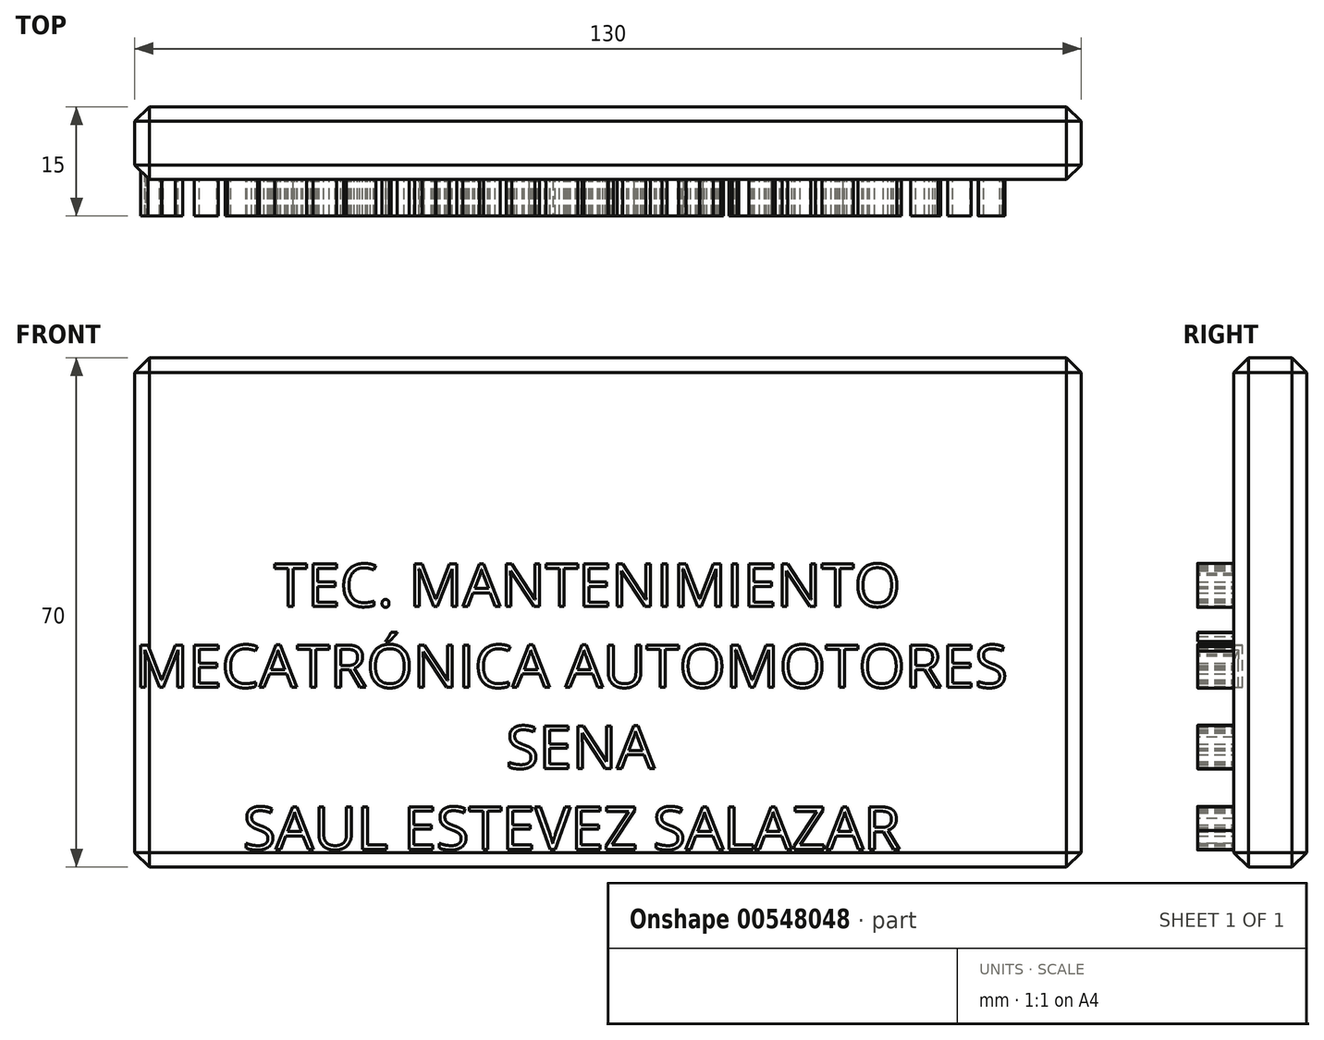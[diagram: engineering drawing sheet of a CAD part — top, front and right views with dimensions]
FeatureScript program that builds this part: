
annotation { "Feature Type Name" : "Feature", "Feature Type Description" : "" }
export const myFeature = defineFeature(function(context is Context, id is Id, definition is map)
    precondition{}
    {
        {
            var Q0;
            Q0=qCreatedBy(makeId("Front.planeOp"),FACE);
            var sketch = newSketch(context, id + "F0", { "sketchPlane" : qUnion([Q0])});
            skLineSegment(sketch, "E0.bottom", {"start": v(-65, 35) * mm, "end": v(65, 35) * mm});
            skLineSegment(sketch, "E0.top", {"start": v(-65, -35) * mm, "end": v(65, -35) * mm});
            skLineSegment(sketch, "E0.left", {"start": v(-65, 35) * mm, "end": v(-65, -35) * mm});
            skLineSegment(sketch, "E0.right", {"start": v(65, 35) * mm, "end": v(65, -35) * mm});
            skPoint(sketch, "E0.middle", {"position": v(0, 0) * mm});
            skSolve(sketch);
        }
        {
            var Q0;
            Q0=makeQuery(id+"F0.imprint","IMPRINT",FACE,{"disambiguationData":[TD([[makeQuery(id+"F0.imprint","IMPRINT",EDGE,{"derivedFrom":sQuery(id+"F0.wireOp",EDGE,"E0.bottom")}),-1.0]])]});
            var sketch = newSketch(context, id + "F1", { "sketchPlane" : qUnion([Q0])});
            skText(sketch, "E1", { "text": "         TEC. MANTENIMIENTO \nMECATRÓNICA AUTOMOTORES \n                        SENA\n       SAUL ESTEVEZ SALAZAR  ", "fontName": "OpenSans-Regular.ttf"});
            const initialGuessF1  = {"E1": [-0.06501, 0.00082, 1, 0, 0.00589]};
            skSetInitialGuess(sketch, initialGuessF1);
            skSolve(sketch);
        }
        {
            var Q0;
            Q0=makeQuery(id+"F0.imprint","IMPRINT",FACE,{"disambiguationData":[TD([[makeQuery(id+"F0.imprint","IMPRINT",EDGE,{"derivedFrom":sQuery(id+"F0.wireOp",EDGE,"E0.bottom")}),-1.0]])]});
            extrude(context, id + "F2", {"entities" : qUnion([Q0]), "oppositeDirection" : true, "depth" : 10 * mm, "offsetDistance" : 25 * mm});
        }
        {
            var Q0;
            Q0 = qSketchRegion(id + "F1", true);
            extrude(context, id + "F3", {"entities" : qUnion([Q0]), "operationType" : NewBodyOperationType.ADD, "endBound" : BoundingType.SYMMETRIC, "depth" : 10 * mm, "offsetDistance" : 25 * mm});
        }
        {
            var Q0;
            Q0=makeQuery(id+"F2.opExtrude","SWEPT_FACE",FACE,{"disambiguationData":[OSD([sQuery(id+"F0.wireOp",EDGE,"E0.left")])]});
            var Q1;
            Q1=makeQuery(id+"F2.opExtrude","SWEPT_FACE",FACE,{"disambiguationData":[OSD([sQuery(id+"F0.wireOp",EDGE,"E0.right")])]});
            var Q2;
            Q2=makeQuery(id+"F2.opExtrude","CAP_EDGE",EDGE,{"disambiguationData":[OSD([sQuery(id+"F0.wireOp",EDGE,"E0.bottom")])],"isStart":false});
            var Q3;
            Q3=makeQuery(id+"F2.opExtrude","SWEPT_FACE",FACE,{"disambiguationData":[OSD([sQuery(id+"F0.wireOp",EDGE,"E0.bottom")])]});
            var Q4;
            Q4=makeQuery(id+"F2.opExtrude","CAP_EDGE",EDGE,{"disambiguationData":[OSD([sQuery(id+"F0.wireOp",EDGE,"E0.top")])],"isStart":false});
            var Q5;
            Q5=makeQuery(id+"F2.opExtrude","SWEPT_FACE",FACE,{"disambiguationData":[OSD([sQuery(id+"F0.wireOp",EDGE,"E0.top")])]});
            chamfer(context, id + "F4", {"entities" : qUnion([Q0, Q1, Q2, Q3, Q4, Q5]), "width" : 2 * mm, "tangentPropagation" : true});
        }
    });
